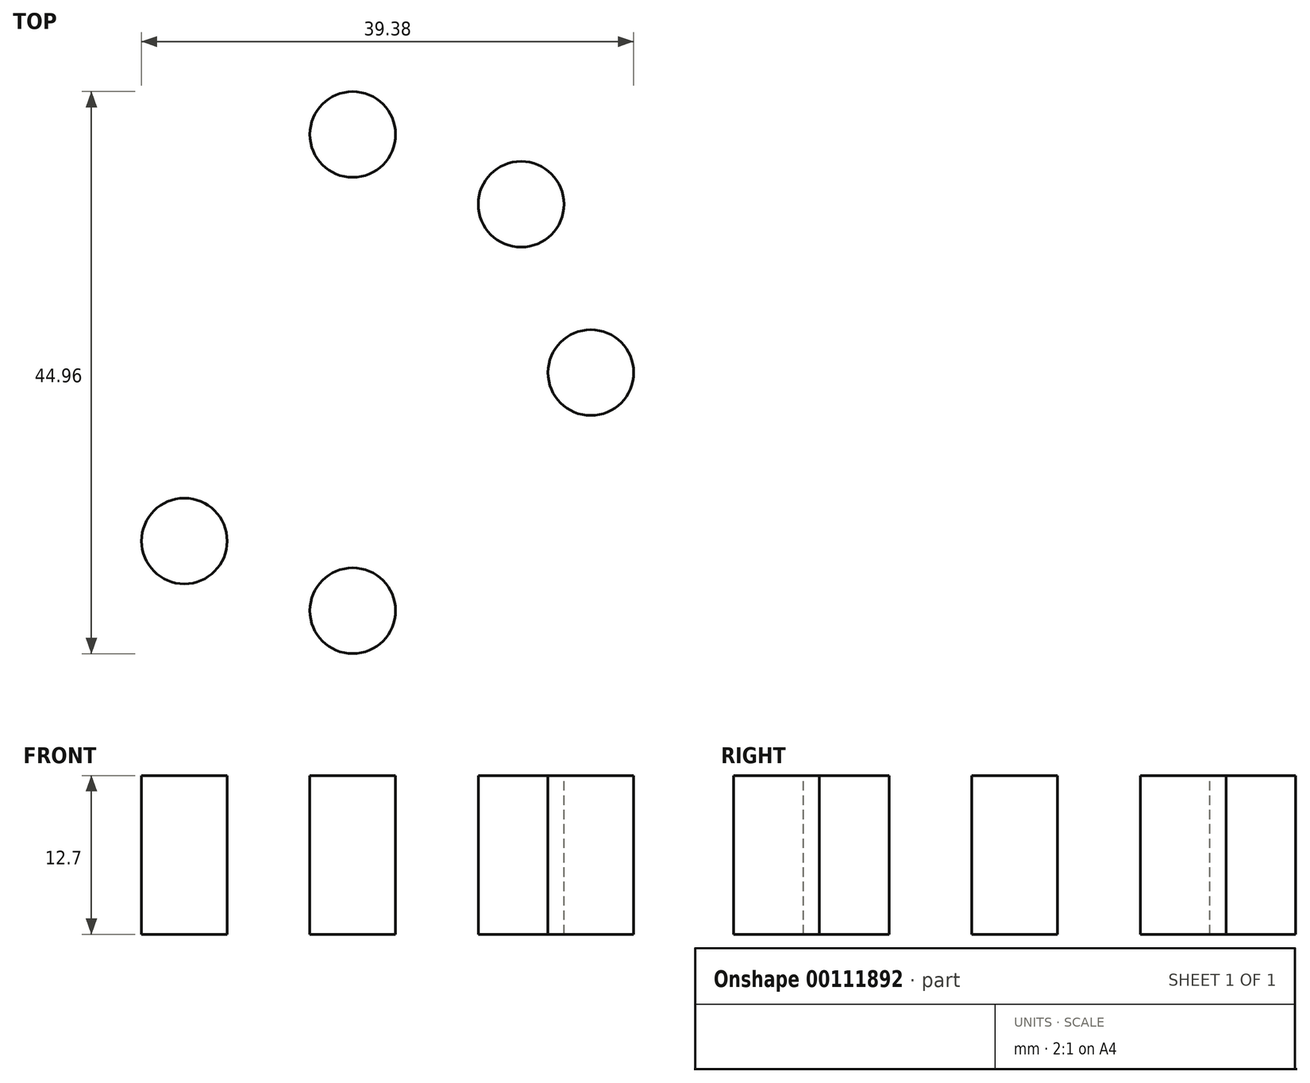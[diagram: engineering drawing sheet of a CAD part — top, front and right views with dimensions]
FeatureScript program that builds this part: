
annotation { "Feature Type Name" : "Feature", "Feature Type Description" : "" }
export const myFeature = defineFeature(function(context is Context, id is Id, definition is map)
    precondition{}
    {
        {
            var Q0;
            Q0=qCreatedBy(makeId("Top.planeOp"),FACE);
            var sketch = newSketch(context, id + "F0", { "sketchPlane" : qUnion([Q0])});
            skLineSegment(sketch, "E0.bottom", {"start": v(63.5, -63.5) * mm, "end": v(-63.5, -63.5) * mm});
            skLineSegment(sketch, "E0.top", {"start": v(63.5, 63.5) * mm, "end": v(-63.5, 63.5) * mm});
            skLineSegment(sketch, "E0.left", {"start": v(63.5, -63.5) * mm, "end": v(63.5, 63.5) * mm});
            skLineSegment(sketch, "E0.right", {"start": v(-63.5, -63.5) * mm, "end": v(-63.5, 63.5) * mm});
            skPoint(sketch, "E0.middle", {"position": v(0, 0) * mm});
            skSolve(sketch);
        }
        {
            var Q0;
            Q0=makeQuery(id+"F0.imprint","IMPRINT",FACE,{"disambiguationData":[TD([[makeQuery(id+"F0.imprint","IMPRINT",EDGE,{"derivedFrom":sQuery(id+"F0.wireOp",EDGE,"E0.bottom")}),-1.0]])]});
            extrude(context, id + "F1", {"entities" : qUnion([Q0]), "depth" : 12.7 * mm});
        }
        {
            var Q0;
            Q0=makeQuery(id+"F1.opExtrude","CAP_FACE",FACE,{"disambiguationData":[OSD([sQuery(id+"F0.wireOp",EDGE,"E0.bottom"),sQuery(id+"F0.wireOp",EDGE,"E0.top"),sQuery(id+"F0.wireOp",EDGE,"E0.left"),sQuery(id+"F0.wireOp",EDGE,"E0.right")])],"isStart":false});
            var sketch = newSketch(context, id + "F2", { "sketchPlane" : qUnion([Q0])});
            skPoint(sketch, "E1", {"position": v(0, 0) * mm});
            skCircle(sketch, "E2", {"center": v(0, -7.7) * mm, "radius": 4.83 * mm});
            skArc(sketch, "E3", {"start": v(-15.67, 3.14) * mm, "mid": v(-17.6, -0.4) * mm, "end": v(-18.74, -4.28) * mm});
            skCircle(sketch, "E4", {"center": v(0, 11.35) * mm, "radius": 3.43 * mm});
            skLineSegment(sketch, "E5", {"start": v(0, -7.7) * mm, "end": v(43, -7.7) * mm, "construction": true});
            skLineSegment(sketch, "E6", {"start": v(0, -7.7) * mm, "end": v(-52.2, -7.7) * mm, "construction": true});
            skCircle(sketch, "E7.MirrorC", {"center": v(0, -26.75) * mm, "radius": 3.43 * mm});
            skArc(sketch, "E8.MirrorC", {"start": v(-10.84, 7.97) * mm, "mid": v(-7.3, 9.9) * mm, "end": v(-3.42, 11.04) * mm});
            skLineSegment(sketch, "E9", {"start": v(0, 19.66) * mm, "end": v(0, -38.4) * mm, "construction": true});
            skCircle(sketch, "E10", {"center": v(-19.05, -7.7) * mm, "radius": 3.43 * mm});
            skCircle(sketch, "E11.MirrorC", {"center": v(19.05, -7.7) * mm, "radius": 3.43 * mm});
            skLineSegment(sketch, "E12", {"start": v(0, -7.7) * mm, "end": v(-19.05, 11.35) * mm, "construction": true});
            skLineSegment(sketch, "E13", {"start": v(0, -7.7) * mm, "end": v(19.05, -26.75) * mm, "construction": true});
            skCircle(sketch, "E14", {"center": v(-13.47, 5.77) * mm, "radius": 3.43 * mm});
            skCircle(sketch, "E15.MirrorC", {"center": v(13.47, 5.77) * mm, "radius": 3.43 * mm});
            skCircle(sketch, "E16.MirrorC", {"center": v(-13.47, -21.17) * mm, "radius": 3.43 * mm});
            skCircle(sketch, "E17.MirrorC", {"center": v(13.47, -21.17) * mm, "radius": 3.43 * mm});
            skArc(sketch, "E18.trimOffspring", {"start": v(-3.42, 11.04) * mm, "mid": v(-7.3, 9.9) * mm, "end": v(-10.84, 7.97) * mm});
            skArc(sketch, "E19.trimOffspring", {"start": v(3.42, 11.04) * mm, "mid": v(7.3, 9.9) * mm, "end": v(10.84, 7.97) * mm});
            skArc(sketch, "E20.trimOffspring", {"start": v(10.84, 7.97) * mm, "mid": v(7.3, 9.9) * mm, "end": v(3.42, 11.04) * mm});
            skArc(sketch, "E21.trimOffspring", {"start": v(15.67, 3.14) * mm, "mid": v(17.6, -0.4) * mm, "end": v(18.74, -4.28) * mm});
            skArc(sketch, "E22.trimOffspring", {"start": v(18.74, -11.11) * mm, "mid": v(17.6, -14.99) * mm, "end": v(15.67, -18.54) * mm});
            skArc(sketch, "E23.trimOffspring", {"start": v(18.74, -4.28) * mm, "mid": v(17.6, -0.4) * mm, "end": v(15.67, 3.14) * mm});
            skArc(sketch, "E24.trimOffspring", {"start": v(15.67, -18.54) * mm, "mid": v(17.6, -14.99) * mm, "end": v(18.74, -11.11) * mm});
            skArc(sketch, "E25.trimOffspring", {"start": v(10.84, -23.37) * mm, "mid": v(7.3, -25.3) * mm, "end": v(3.42, -26.44) * mm});
            skArc(sketch, "E26.trimOffspring", {"start": v(-3.42, -26.44) * mm, "mid": v(-7.3, -25.3) * mm, "end": v(-10.84, -23.37) * mm});
            skArc(sketch, "E27.trimOffspring", {"start": v(-15.67, -18.54) * mm, "mid": v(-17.6, -14.99) * mm, "end": v(-18.74, -11.11) * mm});
            skArc(sketch, "E28.trimOffspring", {"start": v(-10.84, -23.37) * mm, "mid": v(-7.3, -25.3) * mm, "end": v(-3.42, -26.44) * mm});
            skArc(sketch, "E29.trimOffspring", {"start": v(-18.74, -4.28) * mm, "mid": v(-17.6, -0.4) * mm, "end": v(-15.67, 3.14) * mm});
            skArc(sketch, "E30.trimOffspring", {"start": v(-18.74, -11.11) * mm, "mid": v(-17.6, -14.99) * mm, "end": v(-15.67, -18.54) * mm});
            skSolve(sketch);
        }
        {
            var Q0;
            {var subQ0=sQuery(id+"F2.wireOp",EDGE,"E14");var subQ1=makeQuery(id+"F2.imprint","INTERSECT",VERTEX,{"derivedFrom":[subQ0,sQuery(id+"F2.wireOp",EDGE,"E18.trimOffspring")]});Q0=makeQuery(id+"F2.imprint","IMPRINT",FACE,{"disambiguationData":[TD([[makeQuery(id+"F2.imprint","IMPRINT",EDGE,{"disambiguationData":[TD([[subQ1,-1.0]])],"derivedFrom":subQ0}),1.0]])]});}
            var Q1;
            {var subQ0=sQuery(id+"F2.wireOp",EDGE,"E4");var subQ1=makeQuery(id+"F2.imprint","INTERSECT",VERTEX,{"derivedFrom":[subQ0,sQuery(id+"F2.wireOp",EDGE,"E18.trimOffspring")]});Q1=makeQuery(id+"F2.imprint","IMPRINT",FACE,{"disambiguationData":[TD([[makeQuery(id+"F2.imprint","IMPRINT",EDGE,{"disambiguationData":[TD([[subQ1,-1.0]])],"derivedFrom":subQ0}),-1.0]])]});}
            var Q2;
            {var subQ0=sQuery(id+"F2.wireOp",EDGE,"E15.MirrorC");var subQ1=makeQuery(id+"F2.imprint","INTERSECT",VERTEX,{"derivedFrom":[subQ0,sQuery(id+"F2.wireOp",EDGE,"E20.trimOffspring")]});Q2=makeQuery(id+"F2.imprint","IMPRINT",FACE,{"disambiguationData":[TD([[makeQuery(id+"F2.imprint","IMPRINT",EDGE,{"disambiguationData":[TD([[subQ1,-1.0]])],"derivedFrom":subQ0}),-1.0]])]});}
            var Q3;
            {var subQ0=sQuery(id+"F2.wireOp",EDGE,"E11.MirrorC");var subQ1=makeQuery(id+"F2.imprint","INTERSECT",VERTEX,{"derivedFrom":[subQ0,sQuery(id+"F2.wireOp",EDGE,"E23.trimOffspring")]});Q3=makeQuery(id+"F2.imprint","IMPRINT",FACE,{"disambiguationData":[TD([[makeQuery(id+"F2.imprint","IMPRINT",EDGE,{"disambiguationData":[TD([[subQ1,-1.0]])],"derivedFrom":subQ0}),-1.0]])]});}
            var Q4;
            {var subQ0=sQuery(id+"F2.wireOp",EDGE,"E17.MirrorC");var subQ1=makeQuery(id+"F2.imprint","INTERSECT",VERTEX,{"derivedFrom":[subQ0,sQuery(id+"F2.wireOp",EDGE,"E24.trimOffspring")]});Q4=makeQuery(id+"F2.imprint","IMPRINT",FACE,{"disambiguationData":[TD([[makeQuery(id+"F2.imprint","IMPRINT",EDGE,{"disambiguationData":[TD([[subQ1,1.0]])],"derivedFrom":subQ0}),1.0]])]});}
            var Q5;
            {var subQ0=sQuery(id+"F2.wireOp",EDGE,"E7.MirrorC");var subQ1=makeQuery(id+"F2.imprint","INTERSECT",VERTEX,{"derivedFrom":[subQ0,sQuery(id+"F2.wireOp",EDGE,"E25.trimOffspring")]});Q5=makeQuery(id+"F2.imprint","IMPRINT",FACE,{"disambiguationData":[TD([[makeQuery(id+"F2.imprint","IMPRINT",EDGE,{"disambiguationData":[TD([[subQ1,1.0]])],"derivedFrom":subQ0}),-1.0]])]});}
            var Q6;
            {var subQ0=sQuery(id+"F2.wireOp",EDGE,"E16.MirrorC");var subQ1=makeQuery(id+"F2.imprint","INTERSECT",VERTEX,{"derivedFrom":[subQ0,sQuery(id+"F2.wireOp",EDGE,"E28.trimOffspring")]});Q6=makeQuery(id+"F2.imprint","IMPRINT",FACE,{"disambiguationData":[TD([[makeQuery(id+"F2.imprint","IMPRINT",EDGE,{"disambiguationData":[TD([[subQ1,-1.0]])],"derivedFrom":subQ0}),-1.0]])]});}
            var Q7;
            {var subQ0=sQuery(id+"F2.wireOp",EDGE,"E10");var subQ1=makeQuery(id+"F2.imprint","INTERSECT",VERTEX,{"derivedFrom":[subQ0,sQuery(id+"F2.wireOp",EDGE,"E30.trimOffspring")]});Q7=makeQuery(id+"F2.imprint","IMPRINT",FACE,{"disambiguationData":[TD([[makeQuery(id+"F2.imprint","IMPRINT",EDGE,{"disambiguationData":[TD([[subQ1,1.0]])],"derivedFrom":subQ0}),1.0]])]});}
            var Q8;
            Q8=makeQuery(id+"F2.imprint","IMPRINT",FACE,{"disambiguationData":[TD([[makeQuery(id+"F2.imprint","IMPRINT",EDGE,{"derivedFrom":sQuery(id+"F2.wireOp",EDGE,"E2")}),1.0]])]});
            extrude(context, id + "F3", {"entities" : qUnion([Q0, Q1, Q2, Q3, Q4, Q5, Q6, Q7, Q8]), "operationType" : NewBodyOperationType.REMOVE, "oppositeDirection" : true, "depth" : 25.4 * mm});
        }
        {
            var Q0;
            Q0=makeQuery(id+"F1.opExtrude","CAP_FACE",FACE,{"disambiguationData":[OSD([sQuery(id+"F0.wireOp",EDGE,"E0.bottom"),sQuery(id+"F0.wireOp",EDGE,"E0.top"),sQuery(id+"F0.wireOp",EDGE,"E0.left"),sQuery(id+"F0.wireOp",EDGE,"E0.right")])],"isStart":false});
            var sketch = newSketch(context, id + "F4", { "sketchPlane" : qUnion([Q0])});
            skCircle(sketch, "E31", {"center": v(-50.8, -55.88) * mm, "radius": 3.43 * mm});
            skCircle(sketch, "E32", {"center": v(0, 50.8) * mm, "radius": 3.43 * mm});
            skCircle(sketch, "E33", {"center": v(-27.94, -55.88) * mm, "radius": 3.43 * mm});
            skCircle(sketch, "E34.MirrorC", {"center": v(27.94, -55.88) * mm, "radius": 3.43 * mm});
            skCircle(sketch, "E35.MirrorC", {"center": v(50.8, -55.88) * mm, "radius": 3.43 * mm});
            skCircle(sketch, "E36", {"center": v(-53.6, 50.8) * mm, "radius": 3.46 * mm});
            skCircle(sketch, "E37.MirrorC", {"center": v(53.6, 50.8) * mm, "radius": 3.46 * mm});
            skArc(sketch, "E38", {"start": v(-35.81, 54.23) * mm, "mid": v(-39.24, 50.8) * mm, "end": v(-35.81, 47.37) * mm});
            skArc(sketch, "E39.MirrorC", {"start": v(35.81, 54.23) * mm, "mid": v(39.24, 50.8) * mm, "end": v(35.81, 47.37) * mm});
            skArc(sketch, "E40", {"start": v(-22.48, 47.37) * mm, "mid": v(-19.05, 50.8) * mm, "end": v(-22.48, 54.23) * mm});
            skLineSegment(sketch, "E41", {"start": v(-35.81, 47.37) * mm, "end": v(-22.48, 47.37) * mm});
            skLineSegment(sketch, "E42", {"start": v(-35.81, 54.23) * mm, "end": v(-22.48, 54.23) * mm});
            skLineSegment(sketch, "E43.MirrorCS", {"start": v(35.81, 54.23) * mm, "end": v(22.48, 54.23) * mm});
            skLineSegment(sketch, "E44.MirrorCS", {"start": v(35.81, 47.37) * mm, "end": v(22.48, 47.37) * mm});
            skArc(sketch, "E45.MirrorCS", {"start": v(22.48, 47.37) * mm, "mid": v(19.05, 50.8) * mm, "end": v(22.48, 54.23) * mm});
            skSolve(sketch);
        }
        {
            var Q0;
            Q0=makeQuery(id+"F4.imprint","IMPRINT",FACE,{"disambiguationData":[TD([[makeQuery(id+"F4.imprint","IMPRINT",EDGE,{"derivedFrom":sQuery(id+"F4.wireOp",EDGE,"k0NSK73q-ENL1-8xmR-9T86-EbNajhrg5jQ5")}),1.0]])]});
            var Q1;
            Q1=makeQuery(id+"F4.imprint","IMPRINT",FACE,{"disambiguationData":[TD([[makeQuery(id+"F4.imprint","IMPRINT",EDGE,{"derivedFrom":sQuery(id+"F4.wireOp",EDGE,"E32")}),1.0]])]});
            var Q2;
            Q2=makeQuery(id+"F4.imprint","IMPRINT",FACE,{"disambiguationData":[TD([[makeQuery(id+"F4.imprint","IMPRINT",EDGE,{"derivedFrom":sQuery(id+"F4.wireOp",EDGE,"b5a572bb-a2b2-48db-ac8b-7af07611e5600.MirrorC")}),-1.0]])]});
            var Q3;
            Q3=makeQuery(id+"F4.imprint","IMPRINT",FACE,{"disambiguationData":[TD([[makeQuery(id+"F4.imprint","IMPRINT",EDGE,{"derivedFrom":sQuery(id+"F4.wireOp",EDGE,"E34.MirrorC")}),-1.0]])]});
            var Q4;
            Q4=makeQuery(id+"F4.imprint","IMPRINT",FACE,{"disambiguationData":[TD([[makeQuery(id+"F4.imprint","IMPRINT",EDGE,{"derivedFrom":sQuery(id+"F4.wireOp",EDGE,"E35.MirrorC")}),-1.0]])]});
            var Q5;
            Q5=makeQuery(id+"F4.imprint","IMPRINT",FACE,{"disambiguationData":[TD([[makeQuery(id+"F4.imprint","IMPRINT",EDGE,{"derivedFrom":sQuery(id+"F4.wireOp",EDGE,"E31")}),1.0]])]});
            var Q6;
            Q6=makeQuery(id+"F4.imprint","IMPRINT",FACE,{"disambiguationData":[TD([[makeQuery(id+"F4.imprint","IMPRINT",EDGE,{"derivedFrom":sQuery(id+"F4.wireOp",EDGE,"E33")}),1.0]])]});
            var Q7;
            Q7=makeQuery(id+"F4.imprint","IMPRINT",FACE,{"disambiguationData":[TD([[makeQuery(id+"F4.imprint","IMPRINT",EDGE,{"derivedFrom":sQuery(id+"F4.wireOp",EDGE,"E36")}),1.0]])]});
            var Q8;
            Q8=makeQuery(id+"F4.imprint","IMPRINT",FACE,{"disambiguationData":[TD([[makeQuery(id+"F4.imprint","IMPRINT",EDGE,{"derivedFrom":sQuery(id+"F4.wireOp",EDGE,"E37.MirrorC")}),-1.0]])]});
            var Q9;
            Q9=makeQuery(id+"F4.imprint","IMPRINT",FACE,{"disambiguationData":[TD([[makeQuery(id+"F4.imprint","IMPRINT",EDGE,{"derivedFrom":sQuery(id+"F4.wireOp",EDGE,"E38")}),1.0]])]});
            var Q10;
            Q10=makeQuery(id+"F4.imprint","IMPRINT",FACE,{"disambiguationData":[TD([[makeQuery(id+"F4.imprint","IMPRINT",EDGE,{"derivedFrom":sQuery(id+"F4.wireOp",EDGE,"E43.MirrorCS")}),1.0]])]});
            extrude(context, id + "F5", {"entities" : qUnion([Q0, Q1, Q2, Q3, Q4, Q5, Q6, Q7, Q8, Q9, Q10]), "operationType" : NewBodyOperationType.REMOVE, "oppositeDirection" : true, "depth" : 25.4 * mm});
        }
    });
